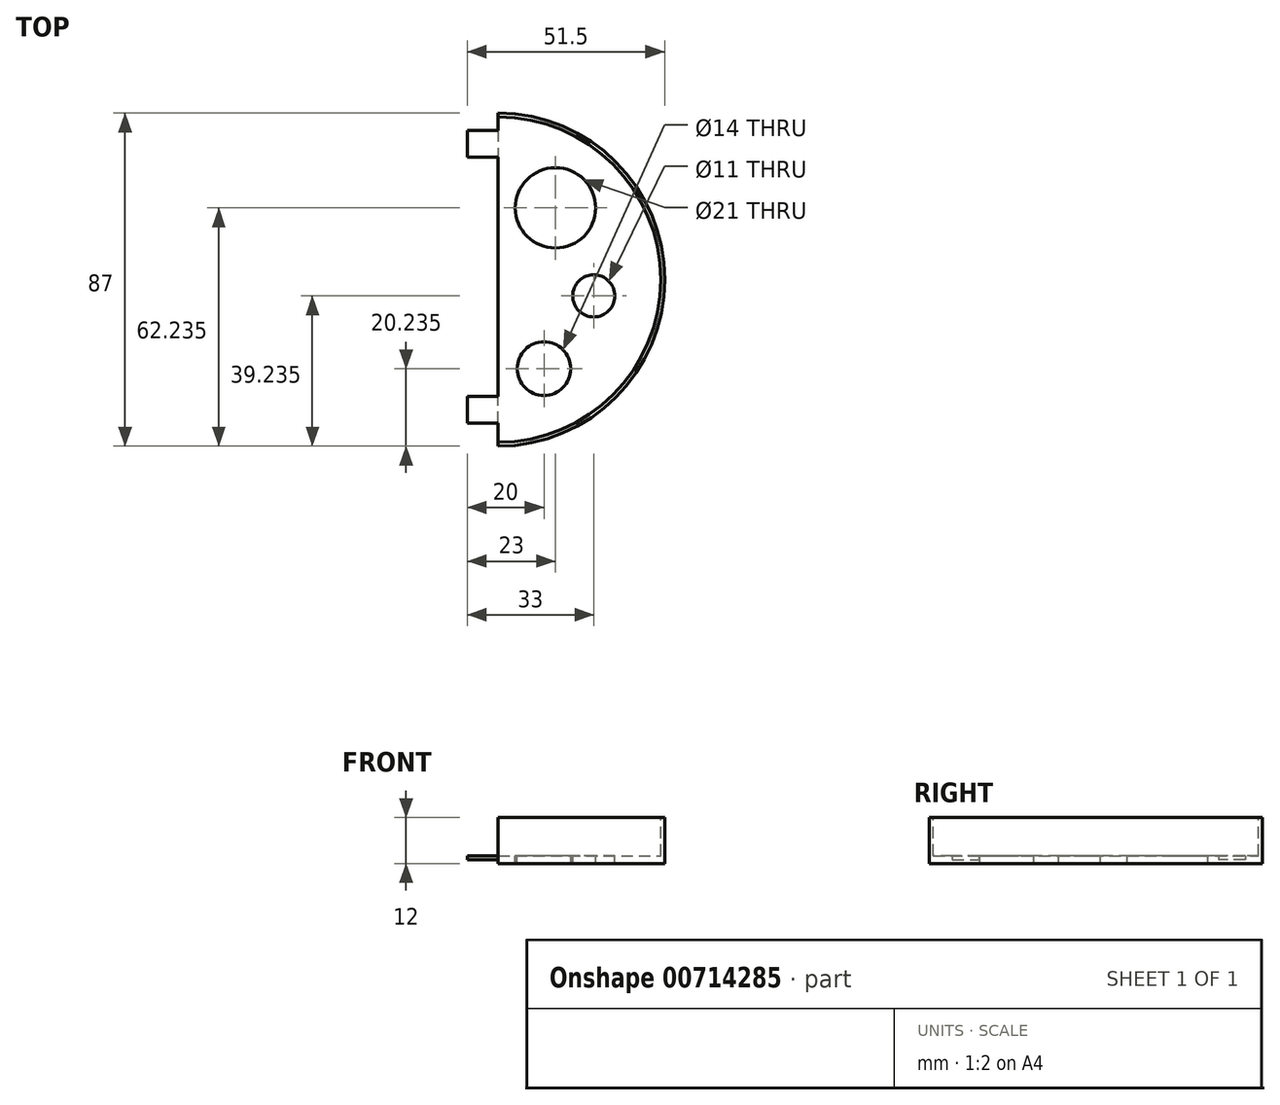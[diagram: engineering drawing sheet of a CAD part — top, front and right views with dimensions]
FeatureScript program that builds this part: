
annotation { "Feature Type Name" : "Feature", "Feature Type Description" : "" }
export const myFeature = defineFeature(function(context is Context, id is Id, definition is map)
    precondition{}
    {
        {
            var Q0;
            Q0=qCreatedBy(makeId("Top.planeOp"),FACE);
            var sketch = newSketch(context, id + "F0", { "sketchPlane" : qUnion([Q0])});
            skArc(sketch, "E0", {"start": v(0, -43.5) * mm, "mid": v(43.5, 0) * mm, "end": v(0, 43.5) * mm});
            skPoint(sketch, "E1", {"position": v(0, 43.5) * mm});
            skPoint(sketch, "E2", {"position": v(0, -43.5) * mm});
            skLineSegment(sketch, "E3", {"start": v(0, 43.5) * mm, "end": v(0, -43.5) * mm});
            skSolve(sketch);
        }
        {
            var Q0;
            Q0=qSketchRegion(id+"F0",true);
            extrude(context, id + "F1", {"entities" : qUnion([Q0]), "depth" : 12 * mm, "offsetDistance" : 25 * mm});
        }
        {
            var Q0;
            Q0=makeQuery(id+"F1.opExtrude","CAP_FACE",FACE,{"disambiguationData":[OSD([sQuery(id+"F0.wireOp",EDGE,"E0")])],"isStart":false});
            var sketch = newSketch(context, id + "F2", { "sketchPlane" : qUnion([Q0])});
            skCircle(sketch, "E4", {"center": v(0, 0) * mm, "radius": 42.5 * mm});
            skSolve(sketch);
        }
        {
            var Q0;
            Q0=qSketchRegion(id+"F2",true);
            extrude(context, id + "F3", {"entities" : qUnion([Q0]), "operationType" : NewBodyOperationType.REMOVE, "oppositeDirection" : true, "depth" : 10 * mm, "offsetDistance" : 25 * mm});
        }
        {
            var Q0;
            Q0=makeQuery(id+"F3.boolean.opBoolean","COPY",FACE,{"derivedFrom":makeQuery(id+"F3.opExtrude","CAP_FACE",FACE,{"disambiguationData":[OSD([sQuery(id+"F2.wireOp",EDGE,"E4")])],"isStart":false})});
            var sketch = newSketch(context, id + "F4", { "sketchPlane" : qUnion([Q0])});
            skCircle(sketch, "E5", {"center": v(-15, 18.73) * mm, "radius": 10.5 * mm});
            skCircle(sketch, "E6", {"center": v(-25, -4.27) * mm, "radius": 5.5 * mm});
            skCircle(sketch, "E7", {"center": v(-12, -23.27) * mm, "radius": 7 * mm});
            skCircle(sketch, "E8.MirrorC", {"center": v(15, 18.73) * mm, "radius": 10.5 * mm});
            skCircle(sketch, "E9.MirrorC", {"center": v(25, -4.27) * mm, "radius": 5.5 * mm});
            skCircle(sketch, "E10.MirrorC", {"center": v(12, -23.27) * mm, "radius": 7 * mm});
            skSolve(sketch);
        }
        {
            var Q0;
            Q0=qSketchRegion(id+"F4",true);
            extrude(context, id + "F5", {"entities" : qUnion([Q0]), "operationType" : NewBodyOperationType.REMOVE, "endBound" : BoundingType.THROUGH_ALL, "oppositeDirection" : true, "depth" : 25 * mm, "offsetDistance" : 25 * mm});
        }
        {
            var Q0;
            Q0=makeQuery(id+"F1.opExtrude","SWEPT_FACE",FACE,{"disambiguationData":[OSD([sQuery(id+"F0.wireOp",EDGE,"E3")])]});
            var sketch = newSketch(context, id + "F6", { "sketchPlane" : qUnion([Q0])});
            skLineSegment(sketch, "E11.bottom", {"start": v(-39, 2) * mm, "end": v(-32, 2) * mm});
            skLineSegment(sketch, "E11.top", {"start": v(-39, 1) * mm, "end": v(-32, 1) * mm});
            skLineSegment(sketch, "E11.left", {"start": v(-39, 2) * mm, "end": v(-39, 1) * mm});
            skLineSegment(sketch, "E11.right", {"start": v(-32, 2) * mm, "end": v(-32, 1) * mm});
            skLineSegment(sketch, "E12.bottom", {"start": v(37.5, 2) * mm, "end": v(30.5, 2) * mm});
            skLineSegment(sketch, "E12.top", {"start": v(37.5, 1) * mm, "end": v(30.5, 1) * mm});
            skLineSegment(sketch, "E12.left", {"start": v(37.5, 2) * mm, "end": v(37.5, 1) * mm});
            skLineSegment(sketch, "E12.right", {"start": v(30.5, 2) * mm, "end": v(30.5, 1) * mm});
            skSolve(sketch);
        }
        {
            var Q0;
            Q0=qSketchRegion(id+"F6",true);
            extrude(context, id + "F7", {"entities" : qUnion([Q0]), "operationType" : NewBodyOperationType.ADD, "depth" : 8 * mm, "offsetDistance" : 25 * mm});
        }
    });
